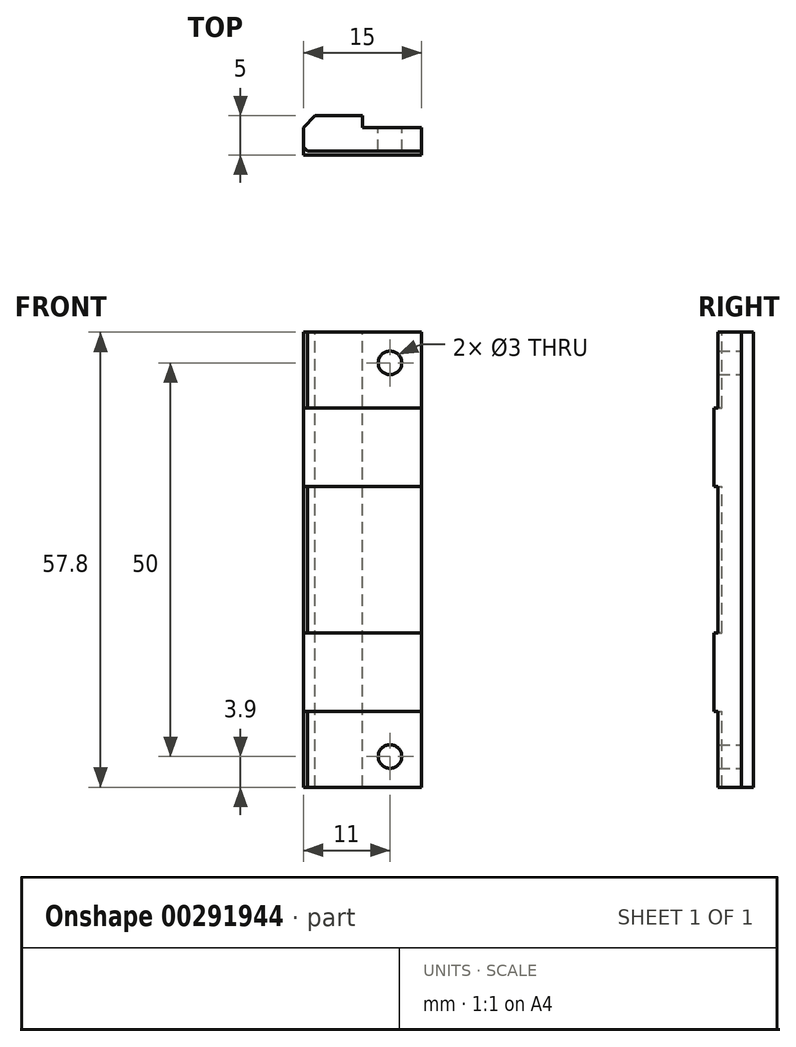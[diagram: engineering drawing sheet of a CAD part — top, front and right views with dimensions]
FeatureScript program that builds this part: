
annotation { "Feature Type Name" : "Feature", "Feature Type Description" : "" }
export const myFeature = defineFeature(function(context is Context, id is Id, definition is map)
    precondition{}
    {
        {
            var Q0;
            Q0=qCreatedBy(makeId("Right.planeOp"),FACE);
            var sketch = newSketch(context, id + "F0", { "sketchPlane" : qUnion([Q0])});
            skLineSegment(sketch, "E0", {"start": v(0, 28.9) * mm, "end": v(3, 28.9) * mm});
            skLineSegment(sketch, "E1", {"start": v(3, 28.9) * mm, "end": v(3, -28.9) * mm});
            skLineSegment(sketch, "E2", {"start": v(3, -28.9) * mm, "end": v(0, -28.9) * mm});
            skLineSegment(sketch, "E3", {"start": v(0, 28.9) * mm, "end": v(0, 24.9) * mm});
            skLineSegment(sketch, "E4", {"start": v(0, 24.9) * mm, "end": v(0, 24.9) * mm});
            skLineSegment(sketch, "E5", {"start": v(0, 24.9) * mm, "end": v(0, -24.9) * mm});
            skLineSegment(sketch, "E6", {"start": v(0, -24.9) * mm, "end": v(0, -24.9) * mm});
            skLineSegment(sketch, "E7", {"start": v(0, -24.9) * mm, "end": v(0, -28.9) * mm});
            skSolve(sketch);
        }
        {
            var Q0;
            Q0=qSketchRegion(id+"F0",true);
            extrude(context, id + "F1", {"entities" : qUnion([Q0]), "depth" : 7.5 * mm, "hasSecondDirection" : true, "secondDirectionOppositeDirection" : true, "secondDirectionDepth" : 7.5 * mm});
        }
        {
            var Q0;
            Q0=makeQuery(id+"F1.opExtrude","SWEPT_FACE",FACE,{"disambiguationData":[OSD([sQuery(id+"F0.wireOp",EDGE,"E1")])]});
            var sketch = newSketch(context, id + "F2", { "sketchPlane" : qUnion([Q0])});
            skCircle(sketch, "E8", {"center": v(-3.5, 25) * mm, "radius": 1.5 * mm});
            skCircle(sketch, "E9", {"center": v(-3.5, -25) * mm, "radius": 1.5 * mm});
            skSolve(sketch);
        }
        {
            var Q0;
            Q0=makeQuery(id+"F1.opExtrude","SWEPT_FACE",FACE,{"disambiguationData":[OSD([sQuery(id+"F0.wireOp",EDGE,"E2")])]});
            var sketch = newSketch(context, id + "F3", { "sketchPlane" : qUnion([Q0])});
            skCircle(sketch, "E10", {"center": v(0, -60) * mm, "radius": 2.5 * mm});
            skSolve(sketch);
        }
        {
            var Q0;
            Q0=qSketchRegion(id+"F3",true);
            extrude(context, id + "F4", {"entities" : qUnion([Q0]), "operationType" : NewBodyOperationType.REMOVE, "oppositeDirection" : true, "depth" : 100 * mm});
        }
        {
            var Q0;
            Q0=makeQuery(id+"F1.opExtrude","SWEPT_FACE",FACE,{"disambiguationData":[OSD([sQuery(id+"F0.wireOp",EDGE,"E1")])]});
            var sketch = newSketch(context, id + "F5", { "sketchPlane" : qUnion([Q0])});
            skCircle(sketch, "E11", {"center": v(-3.5, 31) * mm, "radius": 1.5 * mm});
            skCircle(sketch, "E12", {"center": v(-3.5, -31) * mm, "radius": 1.5 * mm});
            skSolve(sketch);
        }
        {
            var Q0;
            Q0=makeQuery(id+"F1.opExtrude","CAP_FACE",FACE,{"disambiguationData":[OSD([sQuery(id+"F0.wireOp",EDGE,"E0"),sQuery(id+"F0.wireOp",EDGE,"E1"),sQuery(id+"F0.wireOp",EDGE,"E2"),sQuery(id+"F0.wireOp",EDGE,"E3"),sQuery(id+"F0.wireOp",EDGE,"E5"),sQuery(id+"F0.wireOp",EDGE,"E7")])],"isStart":false});
            var sketch = newSketch(context, id + "F6", { "sketchPlane" : qUnion([Q0])});
            skLineSegment(sketch, "E13.bottom", {"start": v(0, 19.29) * mm, "end": v(-0.5, 19.29) * mm});
            skLineSegment(sketch, "E13.top", {"start": v(0, 9.29) * mm, "end": v(-0.5, 9.29) * mm});
            skLineSegment(sketch, "E13.left", {"start": v(0, 19.29) * mm, "end": v(0, 9.29) * mm});
            skLineSegment(sketch, "E13.right", {"start": v(-0.5, 19.29) * mm, "end": v(-0.5, 9.29) * mm});
            skLineSegment(sketch, "E14.bottom", {"start": v(0, -9.29) * mm, "end": v(-0.5, -9.29) * mm});
            skLineSegment(sketch, "E14.top", {"start": v(0, -19.29) * mm, "end": v(-0.5, -19.29) * mm});
            skLineSegment(sketch, "E14.left", {"start": v(0, -9.29) * mm, "end": v(0, -19.29) * mm});
            skLineSegment(sketch, "E14.right", {"start": v(-0.5, -9.29) * mm, "end": v(-0.5, -19.29) * mm});
            skLineSegment(sketch, "E15", {"start": v(-19.13, -14.29) * mm, "end": v(16.5, -14.29) * mm, "construction": true});
            skPoint(sketch, "E15.startSnap0", {"position": v(-0.5, -14.29) * mm});
            skLineSegment(sketch, "E16", {"start": v(-17.07, 14.29) * mm, "end": v(17.48, 14.29) * mm, "construction": true});
            skPoint(sketch, "E16.startSnap0", {"position": v(-0.5, 14.29) * mm});
            skSolve(sketch);
        }
        {
            var Q0;
            Q0=qSketchRegion(id+"F6",true);
            var Q1;
            Q1=makeQuery(id+"F1.opExtrude","CAP_FACE",FACE,{"disambiguationData":[OSD([sQuery(id+"F0.wireOp",EDGE,"E0"),sQuery(id+"F0.wireOp",EDGE,"E1"),sQuery(id+"F0.wireOp",EDGE,"E2"),sQuery(id+"F0.wireOp",EDGE,"E3"),sQuery(id+"F0.wireOp",EDGE,"E5"),sQuery(id+"F0.wireOp",EDGE,"E7")])],"isStart":true});
            extrude(context, id + "F7", {"entities" : qUnion([Q0]), "operationType" : NewBodyOperationType.ADD, "endBound" : BoundingType.UP_TO_SURFACE, "oppositeDirection" : true, "endBoundEntityFace" : qUnion([Q1]), "depth" : 25 * mm});
        }
        {
            var Q0;
            Q0=makeQuery(id+"Fmcx1tmVuyddfUs_2.boolean.opBoolean","MERGE",FACE,{"derivedFrom":[makeQuery(id+"F1.opExtrude","SWEPT_FACE",FACE,{"disambiguationData":[OSD([sQuery(id+"F0.wireOp",EDGE,"E1")])]}),makeQuery(id+"Fmcx1tmVuyddfUs_2.opExtrude","CAP_FACE",FACE,{"disambiguationData":[OSD([sQuery(id+"FtdUe9tOK60J6PF_2.wireOp",EDGE,"JsNW8nu7-rLeb-dfcb-XSDR-FWr7f3ZU8y3m.bottom"),sQuery(id+"FtdUe9tOK60J6PF_2.wireOp",EDGE,"JsNW8nu7-rLeb-dfcb-XSDR-FWr7f3ZU8y3m.top"),sQuery(id+"FtdUe9tOK60J6PF_2.wireOp",EDGE,"JsNW8nu7-rLeb-dfcb-XSDR-FWr7f3ZU8y3m.left"),sQuery(id+"FtdUe9tOK60J6PF_2.wireOp",EDGE,"JsNW8nu7-rLeb-dfcb-XSDR-FWr7f3ZU8y3m.right")])],"isStart":true}),makeQuery(id+"Fmcx1tmVuyddfUs_2.opExtrude","CAP_FACE",FACE,{"disambiguationData":[OSD([sQuery(id+"FtdUe9tOK60J6PF_2.wireOp",EDGE,"ceRr9AZa-OO9h-L4Fo-6wB5-B8ZzmuX6AbRb.bottom"),sQuery(id+"FtdUe9tOK60J6PF_2.wireOp",EDGE,"ceRr9AZa-OO9h-L4Fo-6wB5-B8ZzmuX6AbRb.top"),sQuery(id+"FtdUe9tOK60J6PF_2.wireOp",EDGE,"ceRr9AZa-OO9h-L4Fo-6wB5-B8ZzmuX6AbRb.left"),sQuery(id+"FtdUe9tOK60J6PF_2.wireOp",EDGE,"ceRr9AZa-OO9h-L4Fo-6wB5-B8ZzmuX6AbRb.right")])],"isStart":true})]});
            var sketch = newSketch(context, id + "F8", { "sketchPlane" : qUnion([Q0])});
            skLineSegment(sketch, "E17", {"start": v(0, -35.02) * mm, "end": v(0, 28.9) * mm});
            skSolve(sketch);
        }
        {
            var Q0;
            Q0=qSketchRegion(id+"F2",true);
            extrude(context, id + "F9", {"entities" : qUnion([Q0]), "operationType" : NewBodyOperationType.REMOVE, "oppositeDirection" : true, "depth" : 25 * mm});
        }
        {
            var Q0;
            {var subQ4=sQuery(id+"FtdUe9tOK60J6PF_2.wireOp",EDGE,"JsNW8nu7-rLeb-dfcb-XSDR-FWr7f3ZU8y3m.right");var subQ5=makeQuery(id+"Fmcx1tmVuyddfUs_2.opExtrude","CAP_EDGE",EDGE,{"disambiguationData":[OSD([subQ4])],"isStart":true});Q0=makeQuery(id+"F8.imprint","IMPRINT",FACE,{"disambiguationData":[TD([[makeQuery(id+"F8.imprint","IMPRINT",EDGE,{"derivedFrom":subQ5}),-1.0]])]});}
            var Q1;
            {var subQ1=sQuery(id+"F0.wireOp",EDGE,"E1");var subQ6=makeQuery(id+"F1.opExtrude","CAP_EDGE",EDGE,{"disambiguationData":[OSD([subQ1])],"isStart":true});Q1=makeQuery(id+"F8.imprint","IMPRINT",FACE,{"disambiguationData":[TD([[makeQuery(id+"F8.imprint","IMPRINT",EDGE,{"derivedFrom":subQ6}),-1.0]])]});}
            extrude(context, id + "F10", {"entities" : qUnion([Q0, Q1]), "operationType" : NewBodyOperationType.ADD, "depth" : 1.5 * mm});
        }
        {
            var Q0;
            Q0=makeQuery(id+"F10.opExtrude","CAP_EDGE",EDGE,{"disambiguationData":[OSD([sQuery(id+"FtdUe9tOK60J6PF_2.wireOp",EDGE,"ceRr9AZa-OO9h-L4Fo-6wB5-B8ZzmuX6AbRb.right")])],"isStart":false});
            var Q1;
            {var subQ0=sQuery(id+"FtdUe9tOK60J6PF_2.wireOp",EDGE,"ceRr9AZa-OO9h-L4Fo-6wB5-B8ZzmuX6AbRb.right");var subQ1=sQuery(id+"FtdUe9tOK60J6PF_2.wireOp",EDGE,"ceRr9AZa-OO9h-L4Fo-6wB5-B8ZzmuX6AbRb.left");var subQ2=sQuery(id+"FtdUe9tOK60J6PF_2.wireOp",EDGE,"ceRr9AZa-OO9h-L4Fo-6wB5-B8ZzmuX6AbRb.top");var subQ3=sQuery(id+"FtdUe9tOK60J6PF_2.wireOp",EDGE,"ceRr9AZa-OO9h-L4Fo-6wB5-B8ZzmuX6AbRb.bottom");var subQ4=sQuery(id+"FtdUe9tOK60J6PF_2.wireOp",EDGE,"JsNW8nu7-rLeb-dfcb-XSDR-FWr7f3ZU8y3m.right");var subQ5=sQuery(id+"FtdUe9tOK60J6PF_2.wireOp",EDGE,"JsNW8nu7-rLeb-dfcb-XSDR-FWr7f3ZU8y3m.left");var subQ6=sQuery(id+"FtdUe9tOK60J6PF_2.wireOp",EDGE,"JsNW8nu7-rLeb-dfcb-XSDR-FWr7f3ZU8y3m.top");var subQ7=sQuery(id+"FtdUe9tOK60J6PF_2.wireOp",EDGE,"JsNW8nu7-rLeb-dfcb-XSDR-FWr7f3ZU8y3m.bottom");var subQ8=sQuery(id+"F0.wireOp",EDGE,"E1");Q1=makeQuery(id+"F10.opExtrude","CAP_EDGE",EDGE,{"disambiguationData":[OSD([subQ8,subQ7,subQ6,subQ5,subQ4,subQ3,subQ2,subQ1,subQ0]),TDD([makeQuery(id+"F8.imprint","IMPRINT",EDGE,{"derivedFrom":makeQuery(id+"FqHL6Umb6N44dGH_2.opFillet","BLEND_EDGE",EDGE,{"blendedFrom":[makeQuery(id+"Fmcx1tmVuyddfUs_2.opExtrude","SWEPT_EDGE",EDGE,{"disambiguationData":[OSD([subQ8,subQ2,subQ1])]}),makeQuery(id+"Fmcx1tmVuyddfUs_2.boolean.opBoolean","MERGE",FACE,{"derivedFrom":[makeQuery(id+"F1.opExtrude","SWEPT_FACE",FACE,{"disambiguationData":[OSD([subQ8])]}),makeQuery(id+"Fmcx1tmVuyddfUs_2.opExtrude","CAP_FACE",FACE,{"disambiguationData":[OSD([subQ7,subQ6,subQ5,subQ4])],"isStart":true}),makeQuery(id+"Fmcx1tmVuyddfUs_2.opExtrude","CAP_FACE",FACE,{"disambiguationData":[OSD([subQ3,subQ2,subQ1,subQ0])],"isStart":true})]})],"blendedInto":[makeQuery(id+"Fmcx1tmVuyddfUs_2.boolean.opBoolean","MERGE",FACE,{"derivedFrom":[makeQuery(id+"F1.opExtrude","SWEPT_FACE",FACE,{"disambiguationData":[OSD([subQ8])]}),makeQuery(id+"Fmcx1tmVuyddfUs_2.opExtrude","CAP_FACE",FACE,{"disambiguationData":[OSD([subQ7,subQ6,subQ5,subQ4])],"isStart":true}),makeQuery(id+"Fmcx1tmVuyddfUs_2.opExtrude","CAP_FACE",FACE,{"disambiguationData":[OSD([subQ3,subQ2,subQ1,subQ0])],"isStart":true})]})]})})])],"isStart":false});}
            var Q2;
            Q2=makeQuery(id+"F10.opExtrude","CAP_EDGE",EDGE,{"disambiguationData":[OSD([sQuery(id+"F0.wireOp",EDGE,"E1")])],"isStart":false});
            var Q3;
            {var subQ0=sQuery(id+"FtdUe9tOK60J6PF_2.wireOp",EDGE,"ceRr9AZa-OO9h-L4Fo-6wB5-B8ZzmuX6AbRb.right");var subQ1=sQuery(id+"FtdUe9tOK60J6PF_2.wireOp",EDGE,"ceRr9AZa-OO9h-L4Fo-6wB5-B8ZzmuX6AbRb.left");var subQ2=sQuery(id+"FtdUe9tOK60J6PF_2.wireOp",EDGE,"ceRr9AZa-OO9h-L4Fo-6wB5-B8ZzmuX6AbRb.top");var subQ3=sQuery(id+"FtdUe9tOK60J6PF_2.wireOp",EDGE,"ceRr9AZa-OO9h-L4Fo-6wB5-B8ZzmuX6AbRb.bottom");var subQ4=sQuery(id+"FtdUe9tOK60J6PF_2.wireOp",EDGE,"JsNW8nu7-rLeb-dfcb-XSDR-FWr7f3ZU8y3m.right");var subQ5=sQuery(id+"FtdUe9tOK60J6PF_2.wireOp",EDGE,"JsNW8nu7-rLeb-dfcb-XSDR-FWr7f3ZU8y3m.left");var subQ6=sQuery(id+"FtdUe9tOK60J6PF_2.wireOp",EDGE,"JsNW8nu7-rLeb-dfcb-XSDR-FWr7f3ZU8y3m.top");var subQ7=sQuery(id+"FtdUe9tOK60J6PF_2.wireOp",EDGE,"JsNW8nu7-rLeb-dfcb-XSDR-FWr7f3ZU8y3m.bottom");var subQ8=sQuery(id+"F0.wireOp",EDGE,"E1");Q3=makeQuery(id+"F10.opExtrude","CAP_EDGE",EDGE,{"disambiguationData":[OSD([subQ8,subQ7,subQ6,subQ5,subQ4,subQ3,subQ2,subQ1,subQ0]),TDD([makeQuery(id+"F8.imprint","IMPRINT",EDGE,{"derivedFrom":makeQuery(id+"FqHL6Umb6N44dGH_2.opFillet","BLEND_EDGE",EDGE,{"blendedFrom":[makeQuery(id+"Fmcx1tmVuyddfUs_2.opExtrude","SWEPT_EDGE",EDGE,{"disambiguationData":[OSD([subQ8,subQ6,subQ5])]}),makeQuery(id+"Fmcx1tmVuyddfUs_2.boolean.opBoolean","MERGE",FACE,{"derivedFrom":[makeQuery(id+"F1.opExtrude","SWEPT_FACE",FACE,{"disambiguationData":[OSD([subQ8])]}),makeQuery(id+"Fmcx1tmVuyddfUs_2.opExtrude","CAP_FACE",FACE,{"disambiguationData":[OSD([subQ7,subQ6,subQ5,subQ4])],"isStart":true}),makeQuery(id+"Fmcx1tmVuyddfUs_2.opExtrude","CAP_FACE",FACE,{"disambiguationData":[OSD([subQ3,subQ2,subQ1,subQ0])],"isStart":true})]})],"blendedInto":[makeQuery(id+"Fmcx1tmVuyddfUs_2.boolean.opBoolean","MERGE",FACE,{"derivedFrom":[makeQuery(id+"F1.opExtrude","SWEPT_FACE",FACE,{"disambiguationData":[OSD([subQ8])]}),makeQuery(id+"Fmcx1tmVuyddfUs_2.opExtrude","CAP_FACE",FACE,{"disambiguationData":[OSD([subQ7,subQ6,subQ5,subQ4])],"isStart":true}),makeQuery(id+"Fmcx1tmVuyddfUs_2.opExtrude","CAP_FACE",FACE,{"disambiguationData":[OSD([subQ3,subQ2,subQ1,subQ0])],"isStart":true})]})]})})])],"isStart":false});}
            var Q4;
            Q4=makeQuery(id+"F10.opExtrude","CAP_EDGE",EDGE,{"disambiguationData":[OSD([sQuery(id+"FtdUe9tOK60J6PF_2.wireOp",EDGE,"JsNW8nu7-rLeb-dfcb-XSDR-FWr7f3ZU8y3m.top")])],"isStart":false});
            var Q5;
            Q5=makeQuery(id+"F10.opExtrude","CAP_EDGE",EDGE,{"disambiguationData":[OSD([sQuery(id+"FtdUe9tOK60J6PF_2.wireOp",EDGE,"JsNW8nu7-rLeb-dfcb-XSDR-FWr7f3ZU8y3m.right")])],"isStart":false});
            var Q6;
            Q6=makeQuery(id+"F10.opExtrude","CAP_EDGE",EDGE,{"disambiguationData":[OSD([sQuery(id+"FtdUe9tOK60J6PF_2.wireOp",EDGE,"ceRr9AZa-OO9h-L4Fo-6wB5-B8ZzmuX6AbRb.top")])],"isStart":false});
            chamfer(context, id + "F11", {"entities" : qUnion([Q0, Q1, Q2, Q3, Q4, Q5, Q6]), "width" : 1.5 * mm, "tangentPropagation" : true});
        }
        {
            var Q0;
            Q0=qSketchRegion(id+"F5",true);
            extrude(context, id + "F12", {"entities" : qUnion([Q0]), "operationType" : NewBodyOperationType.REMOVE, "oppositeDirection" : true, "depth" : 25 * mm});
        }
        {
            var Q0;
            {var subQ1=sQuery(id+"F0.wireOp",EDGE,"E7");var subQ2=sQuery(id+"F0.wireOp",EDGE,"E5");var subQ3=sQuery(id+"F0.wireOp",EDGE,"E3");var subQ7=sQuery(id+"F6.wireOp",EDGE,"E13.top");Q0=makeQuery(id+"F7.boolean.opBoolean","SPLIT",EDGE,{"disambiguationData":[TD([makeQuery(id+"F7.opExtrude","SWEPT_FACE",FACE,{"disambiguationData":[OSD([subQ7])]})])],"derivedFrom":makeQuery(id+"F1.opExtrude","CAP_EDGE",EDGE,{"disambiguationData":[OSD([subQ3,subQ2,subQ1])],"isStart":true})});}
            var Q1;
            Q1=makeQuery(id+"F7.opExtrude","TWEAK_EDGE",EDGE,{"derivedFrom":[makeQuery(id+"F1.opExtrude","CAP_FACE",FACE,{"disambiguationData":[OSD([sQuery(id+"F0.wireOp",EDGE,"E0"),sQuery(id+"F0.wireOp",EDGE,"E1"),sQuery(id+"F0.wireOp",EDGE,"E2"),sQuery(id+"F0.wireOp",EDGE,"E3"),sQuery(id+"F0.wireOp",EDGE,"E5"),sQuery(id+"F0.wireOp",EDGE,"E7")])],"isStart":true}),makeQuery(id+"F6.imprint","IMPRINT",EDGE,{"derivedFrom":sQuery(id+"F6.wireOp",EDGE,"E13.right")})]});
            var Q2;
            {var subQ1=sQuery(id+"F0.wireOp",EDGE,"E7");var subQ2=sQuery(id+"F0.wireOp",EDGE,"E5");var subQ3=sQuery(id+"F0.wireOp",EDGE,"E3");var subQ6=sQuery(id+"F0.wireOp",EDGE,"E0");Q2=makeQuery(id+"F7.boolean.opBoolean","SPLIT",EDGE,{"disambiguationData":[TD([makeQuery(id+"F1.opExtrude","SWEPT_FACE",FACE,{"disambiguationData":[OSD([subQ6])]})])],"derivedFrom":makeQuery(id+"F1.opExtrude","CAP_EDGE",EDGE,{"disambiguationData":[OSD([subQ3,subQ2,subQ1])],"isStart":true})});}
            var Q3;
            Q3=makeQuery(id+"F7.opExtrude","TWEAK_EDGE",EDGE,{"derivedFrom":[makeQuery(id+"F1.opExtrude","CAP_FACE",FACE,{"disambiguationData":[OSD([sQuery(id+"F0.wireOp",EDGE,"E0"),sQuery(id+"F0.wireOp",EDGE,"E1"),sQuery(id+"F0.wireOp",EDGE,"E2"),sQuery(id+"F0.wireOp",EDGE,"E3"),sQuery(id+"F0.wireOp",EDGE,"E5"),sQuery(id+"F0.wireOp",EDGE,"E7")])],"isStart":true}),makeQuery(id+"F6.imprint","IMPRINT",EDGE,{"derivedFrom":sQuery(id+"F6.wireOp",EDGE,"E14.right")})]});
            var Q4;
            {var subQ1=sQuery(id+"F0.wireOp",EDGE,"E7");var subQ2=sQuery(id+"F0.wireOp",EDGE,"E5");var subQ3=sQuery(id+"F0.wireOp",EDGE,"E3");var subQ4=sQuery(id+"F0.wireOp",EDGE,"E2");Q4=makeQuery(id+"F7.boolean.opBoolean","SPLIT",EDGE,{"disambiguationData":[TD([makeQuery(id+"F1.opExtrude","SWEPT_FACE",FACE,{"disambiguationData":[OSD([subQ4])]})])],"derivedFrom":makeQuery(id+"F1.opExtrude","CAP_EDGE",EDGE,{"disambiguationData":[OSD([subQ3,subQ2,subQ1])],"isStart":true})});}
            chamfer(context, id + "F13", {"entities" : qUnion([Q0, Q1, Q2, Q3, Q4]), "width" : 0.5 * mm, "tangentPropagation" : true});
        }
    });
